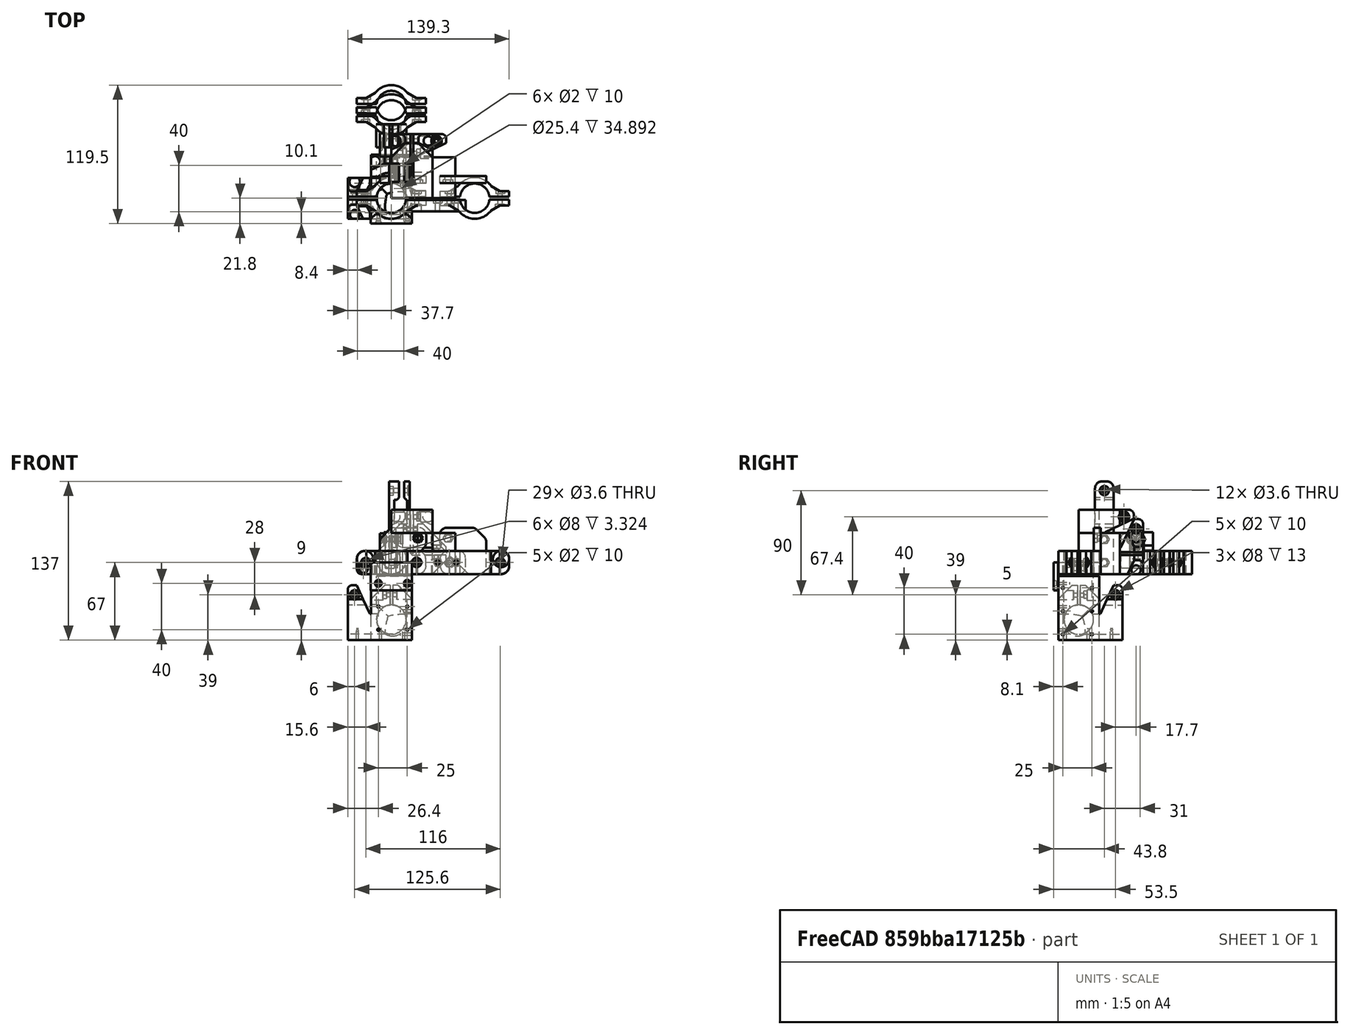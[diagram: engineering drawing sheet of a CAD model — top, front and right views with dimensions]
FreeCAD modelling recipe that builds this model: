
FCSTD DOCUMENT  (FreeCAD 0.19R23578 (Git))
Label: pipe_frame
License: All rights reserved
LicenseURL: http://en.wikipedia.org/wiki/All_rights_reserved
objects: PartDesign::FeatureBase×35, PartDesign::Body×35, Part::MultiFuse×32, Part::Cylinder×31, Part::Box×26, Part::Cut×16, App::Part×10, Part::Fillet×9, Part::Mirroring×8, Part::FeaturePython×7, Part::Chamfer×6, Part::Extrusion×3, Spreadsheet::Sheet×2, Part::Compound×2, Part::Sphere×1, Part::Cone×1
note: 212 computed .brp shape members not serialized (recipe doc carries the construction recipe); baked Part::Feature solids carry a one-line shape summary decoded from their .brp

FEATURE [Part::Cylinder] Cylinder  label="pipe 25mm"
  Angle = 360
  AttacherType = Attacher::AttachEngine3D
  Height = 300
  Radius = 12.7
  expr: Radius = <<p>>.pipe_r
FEATURE [Part::Box] Box001  label="Cube X"
  AttacherType = Attacher::AttachEngine3D
  Height = 35.4
  Length = 20
  Placement = pos=(35.4,0,0) rot=(0,0,1;0rad)
  Width = 35.4
  expr: Length = <<p>>.cube_extra_axis_sz
  expr: Width = <<p>>.cube_wall_sz
  expr: Height = <<p>>.cube_wall_sz
  expr: .Placement.Base.x = <<p>>.cube_wall_sz
FEATURE [Spreadsheet::Sheet] Spreadsheet  label="p"
  cells = A1=pipe_r; B1(pipe_r)=12.7; A2=corner_wall; B2(corner_wall)=5; A3=cube_wall_sz; B3(cube_wall_sz)==2 * pipe_r + 2 * corner_wall; A4=cube_extra_axis_sz; B4(cube_extra_axis_sz)=20; A5=cube_cut_along_sz; B5(cube_cut_along_sz)=2.4; A6=cube_cut_across_sz; B6(cube_cut_across_sz)=30; A7=bolt_squeeze_wall; B7(bolt_squeeze_wall)=5; A8=bolt_squeeze_height; B8(bolt_squeeze_height)=12; A9=profile_10x20_hole_width; B9(profile_10x20_hole_width)=10; A10=profile_10x20_hole_length; B10(profile_10x20_hole_length)=20; A11=cube_profile_width; B11(cube_profile_width)=10; A12=cube_profile_length; B12(cube_profile_length)=20; A13=cube_profile_attachment_height; B13(cube_profile_attachment_height)=40; A14=wall; B14(wall)=3; A15=cube_profile_attachment_length; B15(cube_profile_attachment_length)=16; A16=blocker_circumference; B16(blocker_circumference)==pipe_r * 2 * pi; A17=blocker_r; B17(blocker_r)==pipe_r; A18=blocker_angle; B18(blocker_angle)==blocker_circumference / (blocker_r * 2 * pi / 360) - 30
FEATURE [PartDesign::FeatureBase] Clone
  BaseFeature = -> Cylinder
FEATURE [PartDesign::Body] Body  label="pipe 25mm Z clone"
  BaseFeature = -> Cylinder
  Group = -> [Clone]
  Origin = -> Origin001
  Placement = pos=(17.7,17.7,17.7) rot=(0,0,1;0rad)
  Tip = -> Clone
  expr: .Placement.Base.y = <<p>>.cube_wall_sz / 2
  expr: .Placement.Base.x = <<p>>.cube_wall_sz / 2
  expr: .Placement.Base.z = <<p>>.cube_wall_sz / 2
FEATURE [PartDesign::FeatureBase] Clone001
  BaseFeature = -> Cylinder
FEATURE [PartDesign::Body] Body001  label="pipe 25mm X clone"
  BaseFeature = -> Cylinder
  Group = -> [Clone001]
  Origin = -> Origin002
  Placement = pos=(17.7,17.7,17.7) rot=(0,1,0;1.5708rad)
  Tip = -> Clone001
  expr: .Placement.Base.x = <<p>>.cube_wall_sz / 2
  expr: .Placement.Base.y = <<p>>.cube_wall_sz / 2
  expr: .Placement.Base.z = <<p>>.cube_wall_sz / 2
FEATURE [PartDesign::FeatureBase] Clone002
  BaseFeature = -> Cylinder
FEATURE [PartDesign::Body] Body002  label="pipe 25mm Y clone"
  BaseFeature = -> Cylinder
  Group = -> [Clone002]
  Origin = -> Origin003
  Placement = pos=(17.7,17.7,17.7) rot=(-1,0,0;1.5708rad)
  Tip = -> Clone002
  expr: .Placement.Base.x = <<p>>.cube_wall_sz / 2
  expr: .Placement.Base.y = <<p>>.cube_wall_sz / 2
  expr: .Placement.Base.z = <<p>>.cube_wall_sz / 2
FEATURE [Part::Box] Box002  label="Cube Central"
  AttacherType = Attacher::AttachEngine3D
  Height = 35.4
  Length = 35.4
  Width = 35.4
  expr: Length = <<p>>.cube_wall_sz
  expr: Width = <<p>>.cube_wall_sz
  expr: Height = <<p>>.cube_wall_sz
FEATURE [Part::Box] Box003  label="Cube Y"
  AttacherType = Attacher::AttachEngine3D
  Height = 35.4
  Length = 35.4
  Placement = pos=(0,35.4,0) rot=(0,0,1;0rad)
  Width = 20
  expr: Width = <<p>>.cube_extra_axis_sz
  expr: Height = <<p>>.cube_wall_sz
  expr: Length = <<p>>.cube_wall_sz
  expr: .Placement.Base.y = <<p>>.cube_wall_sz
FEATURE [Part::Box] Box004  label="Cube Z"
  AttacherType = Attacher::AttachEngine3D
  Height = 20
  Length = 35.4
  Placement = pos=(0,0,35.4) rot=(0,0,1;0rad)
  Width = 35.4
  expr: Width = <<p>>.cube_wall_sz
  expr: Height = <<p>>.cube_extra_axis_sz
  expr: .Placement.Base.z = <<p>>.cube_wall_sz
  expr: Length = <<p>>.cube_wall_sz
FEATURE [Part::Box] Box005  label="Cube X body"
  AttacherType = Attacher::AttachEngine3D
  Height = 35.4
  Length = 20
  Width = 35.4
  expr: Length = <<p>>.cube_extra_axis_sz
  expr: Width = <<p>>.cube_wall_sz
  expr: Height = <<p>>.cube_wall_sz
FEATURE [Part::Box] Box006  label="Cube X cut across"
  AttacherType = Attacher::AttachEngine3D
  Height = 35.4
  Length = 30
  Placement = pos=(0,0,22.7) rot=(0,0,1;0rad)
  Width = 35.4
  expr: Width = <<p>>.cube_wall_sz
  expr: Height = <<p>>.cube_wall_sz
  expr: .Placement.Base.z = <<p>>.cube_wall_sz / 2 + 5
  expr: Length = <<p>>.cube_cut_across_sz
FEATURE [Part::Box] Box007  label="Cube X cut along"
  AttacherType = Attacher::AttachEngine3D
  Height = 35.4
  Length = 20
  Placement = pos=(0,16.5,17.7) rot=(0,0,1;0rad)
  Width = 2.4
  expr: Height = <<p>>.cube_wall_sz
  expr: .Placement.Base.z = <<p>>.cube_wall_sz / 2
  expr: Length = <<p>>.cube_extra_axis_sz
  expr: Width = Spreadsheet.cube_cut_along_sz
  expr: .Placement.Base.y = (<<p>>.cube_wall_sz - Spreadsheet.cube_cut_along_sz) / 2
FEATURE [Part::Box] Box008  label="Cube X block along"
  AttacherType = Attacher::AttachEngine3D
  Height = 29.7
  Length = 20
  Placement = pos=(0,0,17.7) rot=(0,0,1;0rad)
  Width = 35.4
  expr: .Placement.Base.z = p001.cube_wall_sz / 2
  expr: Height = <<p>>.cube_wall_sz / 2 + <<p>>.bolt_squeeze_height
  expr: Length = <<p>>.cube_extra_axis_sz
  expr: Width = <<p>>.cube_wall_sz
FEATURE [Part::Extrusion] Extrude003  label="m3 nut hole"
  Dir = (0,0,1)
  DirMode = 2
  FaceMakerClass = Part::FaceMakerBullseye
  LengthFwd = 20
  LengthRev = 0
  Solid = true
  Symmetric = false
FEATURE [PartDesign::FeatureBase] Clone018
  BaseFeature = -> Extrude003
FEATURE [PartDesign::Body] Body020  label="m3 nut hole clone"
  BaseFeature = -> Extrude003
  Group = -> [Clone018]
  Origin = -> Origin040
  Placement = pos=(0,42,0) rot=(1,0,0;1.5708rad)
  Tip = -> Clone018
FEATURE [Part::Cylinder] Cylinder079  label="m3 bolt hole"
  Angle = 360
  AttacherType = Attacher::AttachEngine3D
  Height = 30
  Placement = pos=(0,0,0) rot=(-1,0,0;1.5708rad)
  Radius = 1.8
FEATURE [Part::Sphere] Sphere
  Angle1 = -90
  Angle2 = 90
  Angle3 = 360
  AttacherType = Attacher::AttachEngine3D
  Placement = pos=(16.635,16.635,16.25) rot=(0,0,1;0rad)
  Radius = 12.7
  expr: Radius = <<p>>.pipe_r
FEATURE [Part::MultiFuse] Fusion001  label="pipe fusion"
  Shapes = -> [Body,Body001,Body002,Sphere]
FEATURE [PartDesign::FeatureBase] Clone003
  BaseFeature = -> Fusion001
FEATURE [PartDesign::Body] Body003  label="pipe fusion clone"
  BaseFeature = -> Fusion001
  Group = -> [Clone003]
  Origin = -> Origin004
  Tip = -> Clone003
FEATURE [Part::Cylinder] Cylinder080  label="m3 screw hole"
  Angle = 360
  AttacherType = Attacher::AttachEngine3D
  Height = 10
  Placement = pos=(0,0,0) rot=(0,1,0;1.5708rad)
  Radius = 1
FEATURE [Part::FeaturePython] Array  label="ZY screw hole array"  # Draft array (typed FeaturePython)
  Angle = 360
  ArrayType = 0
  Axis = (0,0,1)
  Base = -> Cylinder080
  Center = (0,0,0)
  Fuse = false
  IntervalAxis = (0,0,0)
  IntervalX = (1,0,0)
  IntervalY = (0,25,0)
  IntervalZ = (0,0,20)
  NumberPolar = 1
  NumberX = 1
  NumberY = 2
  NumberZ = 3
  Placement = pos=(0,4,35) rot=(0,0,1;0rad)
  expr: .IntervalY.y = 25
FEATURE [PartDesign::FeatureBase] Clone024
  BaseFeature = -> Array
  Placement = pos=(0,4,23) rot=(0,0,1;0rad)
FEATURE [PartDesign::Body] Body026  label="Z screw hole array clone"
  BaseFeature = -> Array
  Group = -> [Clone024]
  Origin = -> Origin046
  Placement = pos=(0,0,-14) rot=(0,0,1;0rad)
  Tip = -> Clone024
FEATURE [PartDesign::FeatureBase] Clone025
  BaseFeature = -> Array
  Placement = pos=(0,4,23) rot=(0,0,1;0rad)
FEATURE [PartDesign::Body] Body027  label="Z screw hole array clone001"
  BaseFeature = -> Array
  Group = -> [Clone025]
  Origin = -> Origin047
  Placement = pos=(33,-7e-15,-18) rot=(0,0,1;1.5708rad)
  Tip = -> Clone025
FEATURE [Part::Cylinder] Cylinder081  label="m3 screw hole001"
  Angle = 360
  AttacherType = Attacher::AttachEngine3D
  Height = 10
  Radius = 1
FEATURE [Part::FeaturePython] Array001  label="bottom hole array"  # Draft array (typed FeaturePython)
  Angle = 360
  ArrayType = 0
  Axis = (0,0,1)
  Base = -> Cylinder081
  Center = (0,0,0)
  Fuse = false
  IntervalAxis = (0,0,0)
  IntervalX = (20,0,0)
  IntervalY = (0,20,0)
  IntervalZ = (0,0,1)
  NumberPolar = 1
  NumberX = 3
  NumberY = 3
  NumberZ = 1
  Placement = pos=(6,7,0) rot=(0,0,1;0rad)
FEATURE [Part::MultiFuse] Fusion057  label="pipe extraction fusion"
  Shapes = -> [Body003,Body026,Body027,Array001]
FEATURE [Part::Cylinder] Cylinder082  label="bolt head cylinder"
  Angle = 360
  AttacherType = Attacher::AttachEngine3D
  Height = 20
  Placement = pos=(0,-7,4.9e-15) rot=(-1,0,0;1.5708rad)
  Radius = 4
  expr: .Placement.Base.y = 2 - 2 - 2 - <<p>>.bolt_squeeze_wall
FEATURE [Part::Chamfer] Chamfer  label="Cube X block along chamfer"
  Base = -> Box008
  Edges = 2 edges r=12: [Edge10,Edge12]
FEATURE [Part::Fillet] Fillet  label="Cube X block along fillet"
  Base = -> Chamfer
  Edges = 2 edges r=4: [Edge4,Edge15]
FEATURE [Part::MultiFuse] Fusion002  label="Cube X fusion"
  Shapes = -> [Box005,Fillet]
FEATURE [Part::Box] Box009  label="Cube X cut across extract"
  AttacherType = Attacher::AttachEngine3D
  Height = 100
  Length = 30
  Placement = pos=(-1.55228,0,17.7) rot=(0,1,0;0.436332rad)
  Width = 35.4
  expr: Width = <<p>>.cube_wall_sz
  expr: .Placement.Base.z = <<p>>.cube_wall_sz / 2
  expr: Length = <<p>>.cube_cut_across_sz
FEATURE [Part::Cut] Cut002  label="Cube X cut across extracted"
  Base = -> Box006
  Tool = -> Box009
FEATURE [Part::Cylinder] Cylinder083  label="outer wall"
  Angle = 160
  AttacherType = Attacher::AttachEngine3D
  Height = 20
  Placement = pos=(0,0,0) rot=(0,0,1;0.174533rad)
  Radius = 17.7
  expr: Radius = <<p>>.pipe_r + <<p>>.corner_wall
FEATURE [Part::Cylinder] Cylinder084  label="pile extraction"
  Angle = 360
  AttacherType = Attacher::AttachEngine3D
  Height = 20
  Placement = pos=(0,0,0) rot=(0,0,1;0.174533rad)
  Radius = 12.7
  expr: Radius = <<p>>.pipe_r
FEATURE [Part::Box] Box  label="Cube"
  AttacherType = Attacher::AttachEngine3D
  Height = 20
  Length = 59.4
  Placement = pos=(-29.7,1.2,0) rot=(0,0,1;0rad)
  Width = 5
  expr: Width = <<p>>.bolt_squeeze_wall
  expr: Length = (<<p>>.pipe_r + <<p>>.corner_wall + <<p>>.bolt_squeeze_height) * 2
  expr: .Placement.Base.x = -(<<p>>.pipe_r + <<p>>.corner_wall + <<p>>.bolt_squeeze_height)
  expr: .Placement.Base.y = Spreadsheet.cube_cut_along_sz / 2
FEATURE [Part::Fillet] Fillet001
  Base = -> Box
  Edges = 4 edges r=7: [Edge2,Edge4,Edge6,Edge8]
FEATURE [Part::MultiFuse] Fusion058
  Shapes = -> [Cylinder083,Fillet001]
FEATURE [Part::Cut] Cut003
  Base = -> Fusion058
  Tool = -> Cylinder084
FEATURE [Part::Extrusion] Extrude002  label="m4 nut hole"
  Dir = (0,0,1)
  DirMode = 2
  FaceMakerClass = Part::FaceMakerBullseye
  LengthFwd = 20
  LengthRev = 0
  Solid = true
  Symmetric = false
FEATURE [Part::MultiFuse] Fusion052  label="m4 bolt nut fusion"
  Placement = pos=(23,6,31) rot=(0,0,1;0rad)
FEATURE [Part::Box] Box011  label="Cube002"
  AttacherType = Attacher::AttachEngine3D
  Height = 40
  Length = 40
  Placement = pos=(-10,13,0) rot=(0,0,1;0rad)
  Width = 6
FEATURE [Part::Box] Box012  label="Cube003"
  AttacherType = Attacher::AttachEngine3D
  Height = 60
  Length = 30
  Placement = pos=(-2.22183,13,-7.77817) rot=(0,1,0;0.785398rad)
  Width = 6
FEATURE [Part::Cut] Cut006
  Base = -> Box011
  Tool = -> Box012
FEATURE [Part::Chamfer] Chamfer001
  Base = -> Cut006
  Edges = 1 edges r=10: [Edge2]
FEATURE [Part::Fillet] Fillet002
  Base = -> Chamfer001
  Edges = 6 edges r=6: [Edge2,Edge3,Edge10,Edge13,Edge17,Edge18]
FEATURE [Part::Cut] Cut005  label="side block cut"
  Base = -> Fillet002
  Tool = -> Fusion052
FEATURE [Part::Chamfer] Chamfer002
  Base = -> Cut003
  Edges = 2 edges r=5: [Edge20,Edge30]
FEATURE [Part::Mirroring] Part__Mirroring001  label="Cut003 (Mirror #2)"
  Base = (0,2.86102e-06,10)
  Normal = (0,1,-1.19209e-07)
  Source = -> Chamfer002
FEATURE [Part::MultiFuse] Fusion059
  Shapes = -> [Part__Mirroring001,Chamfer002]
FEATURE [Part::Cylinder] Cylinder085  label="nut cylinder"
  Angle = 360
  AttacherType = Attacher::AttachEngine3D
  Height = 20
  Placement = pos=(0,25,1.9e-14) rot=(-1,0,0;1.5708rad)
  Radius = 4.5
FEATURE [Part::MultiFuse] Fusion056  label="m3 bolt nut fusion"
  Shapes = -> [Cylinder079,Body020,Cylinder082,Cylinder085]
FEATURE [PartDesign::FeatureBase] Clone019
  BaseFeature = -> Fusion056
FEATURE [PartDesign::Body] Body021  label="m3 bolt nut fusion clone"
  BaseFeature = -> Fusion056
  Group = -> [Clone019]
  Origin = -> Origin041
  Placement = pos=(14,0,39) rot=(0,0,1;0rad)
  Tip = -> Clone019
FEATURE [Part::MultiFuse] Fusion003  label="Cube X hole fusion"
  Shapes = -> [Box007,Body021,Cut002]
FEATURE [Part::Cut] Cut001  label="Cube X cut"
  Base = -> Fusion002
  Tool = -> Fusion003
FEATURE [PartDesign::FeatureBase] Clone020
  BaseFeature = -> Cut001
FEATURE [PartDesign::Body] Body022  label="Cube X cut clone X"
  BaseFeature = -> Cut001
  Group = -> [Clone020]
  Origin = -> Origin042
  Placement = pos=(35.4,-8e-15,0) rot=(0,0,1;0rad)
  Tip = -> Clone020
  expr: .Placement.Base.x = <<p>>.cube_wall_sz
FEATURE [PartDesign::FeatureBase] Clone021
  BaseFeature = -> Cut001
FEATURE [PartDesign::Body] Body023  label="Cube X cut clone Y"
  BaseFeature = -> Cut001
  Group = -> [Clone021]
  Origin = -> Origin043
  Placement = pos=(35.4,35.4,3e-15) rot=(0,0,1;1.5708rad)
  Tip = -> Clone021
  expr: .Placement.Base.x = <<p>>.cube_wall_sz
  expr: .Placement.Base.y = <<p>>.cube_wall_sz
FEATURE [PartDesign::FeatureBase] Clone022
  BaseFeature = -> Cut001
FEATURE [PartDesign::Body] Body024  label="Cube X cut clone Z"
  BaseFeature = -> Cut001
  Group = -> [Clone022]
  Origin = -> Origin044
  Placement = pos=(-1.6e-14,-4e-15,35.4) rot=(0.57735,0.57735,0.57735;4.18879rad)
  Tip = -> Clone022
  expr: .Placement.Base.z = <<p>>.cube_wall_sz
FEATURE [Part::Mirroring] Part__Mirroring  label="Cube X cut (Mirror #1)"
  Base = (0,0,0)
  Normal = (0,1,0)
  Source = -> Cut001
FEATURE [PartDesign::FeatureBase] Clone023
  BaseFeature = -> Cut001
FEATURE [PartDesign::Body] Body025  label="Cube X cut clone Y001"
  BaseFeature = -> Cut001
  Group = -> [Clone023]
  Origin = -> Origin045
  Placement = pos=(0,35.4,0) rot=(0.57735,0.57735,0.57735;2.0944rad)
  Tip = -> Clone023
  expr: .Placement.Base.y = <<p>>.cube_wall_sz
FEATURE [PartDesign::FeatureBase] Clone026
  BaseFeature = -> Part__Mirroring
FEATURE [PartDesign::Body] Body028  label="Cube X cut (Mirror #1) Y"
  BaseFeature = -> Part__Mirroring
  Group = -> [Clone026]
  Origin = -> Origin048
  Placement = pos=(7e-15,35.4,0) rot=(0,0,1;1.5708rad)
  Tip = -> Clone026
  expr: .Placement.Base.y = <<p>>.cube_wall_sz
FEATURE [Part::MultiFuse] Fusion  label="corner fusion"
  Shapes = -> [Box002,Box004,Body022,Body028]
FEATURE [Part::Cut] Cut  label="pipe cut"
  Base = -> Fusion
  Tool = -> Fusion057
FEATURE [App::Part] Part  label="corner part"
  Group = -> [Box001,Box002,Box003,Box004,Fusion,Body003,Cut,Body022,Body023,Body024,Body025,Body026,Cut001,Fusion003,Part__Mirroring,Fusion001,Body021,Fusion002,Body002,Body001,Cylinder,Body,Box005,Box006,Box007,Box008,Sphere,Fillet,Fusion057,Body027,Cylinder081,Array001]
  Origin = -> Origin
FEATURE [PartDesign::FeatureBase] Clone028
  BaseFeature = -> Fusion056
FEATURE [PartDesign::Body] Body030  label="m3 bolt nut fusion clone002"
  BaseFeature = -> Fusion056
  Group = -> [Clone028]
  Origin = -> Origin051
  Placement = pos=(-22,0,10) rot=(0,0,1;0rad)
  Tip = -> Clone028
FEATURE [Part::Mirroring] Part__Mirroring002  label="m3 bolt nut fusion clone002 (Mirror #3)"
  Base = (9.53674e-07,17.5,10)
  Normal = (1,0,-1.19209e-07)
  Source = -> Body030
FEATURE [Part::MultiFuse] Fusion062  label="m3 bolt nut fusion002"
  Placement = pos=(0,-18,0) rot=(0,0,1;0rad)
  Shapes = -> [Part__Mirroring002,Body030]
FEATURE [Part::Cut] Cut004  label="tube block cut"
  Base = -> Fusion059
  Tool = -> Fusion062
FEATURE [Part::Compound] Compound  label="attach part compound"
  Links = -> [Cut004,Cut005]
FEATURE [PartDesign::FeatureBase] Clone029
  BaseFeature = -> Cut004
FEATURE [PartDesign::Body] Body031  label="tube block cut clone"
  BaseFeature = -> Cut004
  Group = -> [Clone029]
  Origin = -> Origin053
  Tip = -> Clone029
FEATURE [Part::Box] Box039  label="profile 20x10 holder cube"
  AttacherType = Attacher::AttachEngine3D
  Height = 35
  Length = 20
  Placement = pos=(-10,16,0) rot=(0,0,1;0rad)
  Width = 20
  expr: Length = 2 * <<p>>.corner_wall + <<p>>.profile_10x20_hole_width
  expr: .Placement.Base.x = -(2 * <<p>>.corner_wall + <<p>>.profile_10x20_hole_width) / 2
  expr: Height = <<p>>.corner_wall + <<p>>.profile_10x20_hole_length + 10
FEATURE [Part::Box] Box040  label="profile 20x10 extraction hole"
  AttacherType = Attacher::AttachEngine3D
  Height = 70
  Length = 10
  Placement = pos=(-5,16,5) rot=(0,0,1;0rad)
  Width = 50
  expr: Height = <<p>>.profile_10x20_hole_length + 50
  expr: .Placement.Base.z = <<p>>.corner_wall
  expr: Length = <<p>>.profile_10x20_hole_width
FEATURE [Part::Fillet] Fillet003
  Base = -> Box039
  Edges = 2 edges r=5: [Edge10,Edge12]
FEATURE [Part::Cylinder] Cylinder086  label="m3 bolt hole001"
  Angle = 360
  AttacherType = Attacher::AttachEngine3D
  Height = 30
  Placement = pos=(0,0,0) rot=(-1,0,0;1.5708rad)
  Radius = 1.8
FEATURE [PartDesign::FeatureBase] Clone030
  BaseFeature = -> Extrude003
FEATURE [PartDesign::Body] Body032  label="m3 nut hole clone001"
  BaseFeature = -> Extrude003
  Group = -> [Clone030]
  Origin = -> Origin054
  Placement = pos=(0,42,0) rot=(1,0,0;1.5708rad)
  Tip = -> Clone030
FEATURE [Part::Cylinder] Cylinder087  label="bolt head cylinder002"
  Angle = 360
  AttacherType = Attacher::AttachEngine3D
  Height = 20
  Placement = pos=(0,-14,3e-15) rot=(-1,0,0;1.5708rad)
  Radius = 4
FEATURE [Part::Cylinder] Cylinder088  label="bolt head cylinder003"
  Angle = 360
  AttacherType = Attacher::AttachEngine3D
  Height = 20
  Placement = pos=(0,25,3.48e-14) rot=(-1,0,0;1.5708rad)
  Radius = 4.5
FEATURE [Part::MultiFuse] Fusion063  label="m3 bolt nut fusion003"
  Shapes = -> [Cylinder086,Body032,Cylinder087,Cylinder088]
FEATURE [PartDesign::FeatureBase] Clone031
  BaseFeature = -> Fusion063
FEATURE [PartDesign::Body] Body033  label="m3 bolt nut fusion003 clone"
  BaseFeature = -> Fusion063
  Group = -> [Clone031]
  Origin = -> Origin055
  Placement = pos=(14,27,30) rot=(0,0,1;1.5708rad)
  Tip = -> Clone031
  expr: .Placement.Base.z = <<p>>.corner_wall + <<p>>.profile_10x20_hole_length + 5
FEATURE [App::Part] Part003  label="m3 bold nut fusion part"
  Group = -> [Cylinder086,Body032,Cylinder087,Cylinder088,Fusion063]
  Origin = -> Origin056
FEATURE [Part::MultiFuse] Fusion064  label="profile holder extraction fusion"
  Shapes = -> [Box040,Body033]
FEATURE [Part::Mirroring] Part__Mirroring004  label="attach part compound (Mirror #5)"
  Base = (36,0,0)
  Normal = (1,0,0)
  Source = -> Compound
FEATURE [App::Part] Part001  label="25mm_attach part"
  Group = -> [Cylinder083,Cylinder084,Cut003,Box,Fusion058,Fillet001,Part__Mirroring001,Fusion059,Body030,Cut004,Fusion052,Fillet002,Box011,Cut005,Chamfer001,Box012,Cut006,Part__Mirroring002,Fusion062,Compound,Chamfer002,Fusion056,Body020,Cylinder079,Cylinder082,Cylinder085,Part__Mirroring004]
  Origin = -> Origin049
FEATURE [Part::MultiFuse] Fusion065
  Shapes = -> [Fillet003,Body031]
FEATURE [Part::Cut] Cut007  label="profile holder cut"
  Base = -> Fusion065
  Tool = -> Fusion064
FEATURE [Part::Mirroring] Part__Mirroring003  label="profile holder cut (Mirror #4)"
  Base = (0,36,0)
  Normal = (0,1,0)
  Source = -> Cut007
FEATURE [App::Part] Part002  label="25mm side pipe attach part"
  Group = -> [Body031,Box039,Box040,Fillet003,Cut007,Body033,Fusion064,Part__Mirroring003,Fusion065]
  Origin = -> Origin052
FEATURE [Part::Box] Box042  label="attachment extraction"
  AttacherType = Attacher::AttachEngine3D
  Height = 40
  Length = 20
  Placement = pos=(20,5,0) rot=(0,0,1;0rad)
  Width = 4.3
  expr: Height = <<p>>.cube_profile_attachment_height
FEATURE [PartDesign::FeatureBase] Clone011
  BaseFeature = -> Extrude002
FEATURE [PartDesign::Body] Body013  label="m4 nut hole clone"
  BaseFeature = -> Extrude002
  Group = -> [Clone011]
  Placement = pos=(0,-10,0) rot=(-1,0,0;1.5708rad)
  Tip = -> Clone011
FEATURE [Part::Cylinder] Cylinder077  label="m4 bolt hole"
  Angle = 360
  AttacherType = Attacher::AttachEngine3D
  Height = 30
  Placement = pos=(0,0,0) rot=(-1,0,0;1.5708rad)
  Radius = 2.6
FEATURE [Part::MultiFuse] Fusion067  label="m4 bolt nut fusion001"
  Shapes = -> [Cylinder077,Body013]
FEATURE [Part::FeaturePython] Array001042  label="m4 bolt hole array"  # Draft array (typed FeaturePython)
  Angle = 360
  ArrayType = 0
  Axis = (0,0,1)
  Base = -> Fusion067
  Center = (0,0,0)
  Fuse = false
  IntervalAxis = (0,0,0)
  IntervalX = (1,0,0)
  IntervalY = (0,1,0)
  IntervalZ = (0,0,20)
  NumberPolar = 1
  NumberX = 1
  NumberY = 1
  NumberZ = 2
  Placement = pos=(13,25,10) rot=(0,0,1;1.5708rad)
FEATURE [Part::Box] Box041  label="attachment internal cube"
  AttacherType = Attacher::AttachEngine3D
  Height = 40
  Length = 21
  Placement = pos=(3,2.5,0) rot=(0,0,1;0rad)
  Width = 11
  expr: Length = <<p>>.cube_profile_length + 1
  expr: Width = <<p>>.cube_profile_width + 1
  expr: Height = <<p>>.cube_profile_attachment_height
  expr: .Placement.Base.x = <<p>>.wall
  expr: .Placement.Base.y = <<p>>.wall - 0.5
FEATURE [Part::Box] Box045  label="attachment external cube"
  AttacherType = Attacher::AttachEngine3D
  Height = 16
  Length = 40
  Width = 18
  expr: Length = <<p>>.cube_profile_length + 2 * <<p>>.wall + 14
  expr: Width = <<p>>.cube_profile_width + 2 * <<p>>.wall + 2
  expr: Height = <<p>>.cube_profile_attachment_length
FEATURE [PartDesign::FeatureBase] Clone033
  BaseFeature = -> Extrude002
FEATURE [PartDesign::Body] Body035  label="m4 nut hole clone001"
  BaseFeature = -> Extrude002
  Group = -> [Clone033]
  Placement = pos=(0,-10,0) rot=(-1,0,0;1.5708rad)
  Tip = -> Clone033
FEATURE [Part::Cylinder] Cylinder090  label="m4 bolt hole001"
  Angle = 360
  AttacherType = Attacher::AttachEngine3D
  Height = 30
  Placement = pos=(0,0,0) rot=(-1,0,0;1.5708rad)
  Radius = 2.6
FEATURE [Part::MultiFuse] Fusion068  label="m4 bolt nut fusion002"
  Shapes = -> [Cylinder090,Body035]
FEATURE [Part::FeaturePython] Array001045  label="m4 bolt hole array001"  # Draft array (typed FeaturePython)
  Angle = 360
  ArrayType = 0
  Axis = (0,0,1)
  Base = -> Fusion068
  Center = (0,0,0)
  Fuse = false
  IntervalAxis = (0,0,0)
  IntervalX = (1,0,0)
  IntervalY = (0,1,0)
  IntervalZ = (0,0,20)
  NumberPolar = 1
  NumberX = 1
  NumberY = 1
  NumberZ = 2
  Placement = pos=(13,22,10) rot=(0,0,1;1.5708rad)
FEATURE [Part::Box] Box046  label="frame attachment cube001"
  AttacherType = Attacher::AttachEngine3D
  Height = 40
  Length = 6
  Placement = pos=(-2,14,0) rot=(0,0,1;0rad)
  Width = 16
  expr: Height = <<p>>.cube_profile_attachment_height
  expr: Width = <<p>>.cube_profile_attachment_length
FEATURE [Part::Cut] Cut023014  label="frame attach cut"
  Base = -> Box046
  Tool = -> Array001045
FEATURE [Part::Cylinder] Cylinder091  label="m3 bolt hole003"
  Angle = 360
  AttacherType = Attacher::AttachEngine3D
  Height = 30
  Placement = pos=(0,0,0) rot=(-1,0,0;1.5708rad)
  Radius = 1.8
FEATURE [PartDesign::FeatureBase] Clone034
  BaseFeature = -> Extrude003
FEATURE [PartDesign::Body] Body036  label="m3 nut hole clone003"
  BaseFeature = -> Extrude003
  Group = -> [Clone034]
  Origin = -> Origin059
  Placement = pos=(0,42,0) rot=(1,0,0;1.5708rad)
  Tip = -> Clone034
FEATURE [Part::Cylinder] Cylinder092  label="bolt head cylinder004"
  Angle = 360
  AttacherType = Attacher::AttachEngine3D
  Height = 20
  Placement = pos=(0,-7,5e-15) rot=(-1,0,0;1.5708rad)
  Radius = 4
FEATURE [Part::Cylinder] Cylinder093  label="bolt head cylinder005"
  Angle = 360
  AttacherType = Attacher::AttachEngine3D
  Height = 20
  Placement = pos=(0,-7,3.32e-14) rot=(-1,0,0;1.5708rad)
  Radius = 4.5
  expr: .Placement.Base.y = 2 - 2 - 2 - <<p>>.bolt_squeeze_wall
FEATURE [Part::MultiFuse] Fusion070  label="m3 bolt nut fusion005"
  Shapes = -> [Cylinder091,Body036,Cylinder092,Cylinder093]
FEATURE [Spreadsheet::Sheet] Spreadsheet001  label="p0"
  cells = A1=pipe_r; B1(pipe_r)=12.7; A2=corner_wall; B2(corner_wall)=5; A3=cube_wall_sz; B3(cube_wall_sz)==2 * pipe_r + 2 * corner_wall; A4=cube_extra_axis_sz; B4(cube_extra_axis_sz)=20; A5=cube_cut_along_sz; B5(cube_cut_along_sz)=3; A6=cube_cut_across_sz; B6(cube_cut_across_sz)=30; A7=bolt_squeeze_wall; B7(bolt_squeeze_wall)=5; A8=bolt_squeeze_height; B8(bolt_squeeze_height)=12; A9=profile_10x20_hole_width; B9(profile_10x20_hole_width)=10; A10=profile_10x20_hole_length; B10(profile_10x20_hole_length)=20; A11=cube_profile_width; B11(cube_profile_width)=10; A12=cube_profile_length; B12(cube_profile_length)=20; A13=cube_profile_attachment_height; B13(cube_profile_attachment_height)=40; A14=wall; B14(wall)=3; A15=cube_profile_attachment_length; B15(cube_profile_attachment_length)=16
FEATURE [Part::Extrusion] Extrude004  label="m3 nut hole001"
  Dir = (0,0,1)
  DirMode = 2
  FaceMakerClass = Part::FaceMakerBullseye
  LengthFwd = 20
  LengthRev = 0
  Solid = true
  Symmetric = false
FEATURE [PartDesign::FeatureBase] Clone036
  BaseFeature = -> Extrude004
FEATURE [PartDesign::Body] Body038  label="m3 nut hole clone004"
  BaseFeature = -> Extrude004
  Group = -> [Clone036]
  Origin = -> Origin061
  Placement = pos=(0,42,0) rot=(1,0,0;1.5708rad)
  Tip = -> Clone036
FEATURE [Part::Cylinder] Cylinder094  label="m3 bolt hole004"
  Angle = 360
  AttacherType = Attacher::AttachEngine3D
  Height = 30
  Placement = pos=(0,0,0) rot=(-1,0,0;1.5708rad)
  Radius = 1.8
FEATURE [Part::Cylinder] Cylinder095  label="bolt head cylinder006"
  Angle = 360
  AttacherType = Attacher::AttachEngine3D
  Height = 20
  Placement = pos=(0,-7,4.9e-15) rot=(-1,0,0;1.5708rad)
  Radius = 4
  expr: .Placement.Base.y = 2 - 2 - 2 - <<p>>.bolt_squeeze_wall
FEATURE [Part::Cylinder] Cylinder096  label="outer wall001"
  Angle = 160
  AttacherType = Attacher::AttachEngine3D
  Height = 20
  Placement = pos=(0,0,0) rot=(0,0,1;0.174533rad)
  Radius = 17.7
  expr: Radius = <<p>>.pipe_r + <<p>>.corner_wall
FEATURE [Part::Cylinder] Cylinder097  label="pile extraction001"
  Angle = 360
  AttacherType = Attacher::AttachEngine3D
  Height = 20
  Placement = pos=(0,0,0) rot=(0,0,1;0.174533rad)
  Radius = 12.7
  expr: Radius = <<p>>.pipe_r
FEATURE [Part::Box] Box047  label="Cube004"
  AttacherType = Attacher::AttachEngine3D
  Height = 20
  Length = 59.4
  Placement = pos=(-29.7,1.5,0) rot=(0,0,1;0rad)
  Width = 5
  expr: Width = <<p>>.bolt_squeeze_wall
  expr: Length = (<<p>>.pipe_r + <<p>>.corner_wall + <<p>>.bolt_squeeze_height) * 2
  expr: .Placement.Base.x = -(<<p>>.pipe_r + <<p>>.corner_wall + <<p>>.bolt_squeeze_height)
  expr: .Placement.Base.y = Spreadsheet001.cube_cut_along_sz / 2
FEATURE [Part::Fillet] Fillet022
  Base = -> Box047
  Edges = 4 edges r=7: [Edge2,Edge4,Edge6,Edge8]
FEATURE [Part::MultiFuse] Fusion072
  Shapes = -> [Cylinder096,Fillet022]
FEATURE [Part::Cut] Cut023016
  Base = -> Fusion072
  Tool = -> Cylinder097
FEATURE [Part::Chamfer] Chamfer004
  Base = -> Cut023016
  Edges = 2 edges r=5: [Edge20,Edge30]
FEATURE [Part::Mirroring] Part__Mirroring005  label="Cut003 (Mirror #2)001"
  Base = (0,2.86102e-06,10)
  Normal = (0,1,-1.19209e-07)
  Source = -> Chamfer004
FEATURE [Part::MultiFuse] Fusion073
  Shapes = -> [Part__Mirroring005,Chamfer004]
FEATURE [Part::Cylinder] Cylinder098  label="nut cylinder001"
  Angle = 360
  AttacherType = Attacher::AttachEngine3D
  Height = 20
  Placement = pos=(0,25,1.9e-14) rot=(-1,0,0;1.5708rad)
  Radius = 4.5
FEATURE [Part::MultiFuse] Fusion071  label="m3 bolt nut fusion006"
  Shapes = -> [Cylinder094,Body038,Cylinder095,Cylinder098]
FEATURE [PartDesign::FeatureBase] Clone037
  BaseFeature = -> Fusion071
FEATURE [PartDesign::Body] Body039  label="m3 bolt nut fusion clone003"
  BaseFeature = -> Fusion071
  Group = -> [Clone037]
  Origin = -> Origin062
  Placement = pos=(-22,0,10) rot=(0,0,1;0rad)
  Tip = -> Clone037
FEATURE [Part::Mirroring] Part__Mirroring006  label="m3 bolt nut fusion clone002 (Mirror #3)001"
  Base = (9.53674e-07,17.5,10)
  Normal = (1,0,-1.19209e-07)
  Source = -> Body039
FEATURE [Part::MultiFuse] Fusion074  label="m3 bolt nut fusion007"
  Placement = pos=(0,-18,0) rot=(0,0,1;0rad)
  Shapes = -> [Part__Mirroring006,Body039]
FEATURE [Part::Cut] Cut023015  label="tube block cut001"
  Base = -> Fusion073
  Tool = -> Fusion074
FEATURE [PartDesign::FeatureBase] Clone038
  BaseFeature = -> Cut023015
FEATURE [PartDesign::Body] Body040  label="tube block cut clone001"
  BaseFeature = -> Cut023015
  Group = -> [Clone038]
  Origin = -> Origin064
  Tip = -> Clone038
FEATURE [Part::Cylinder] Cylinder099  label="m3 bolt hole005"
  Angle = 360
  AttacherType = Attacher::AttachEngine3D
  Height = 30
  Placement = pos=(0,0,0) rot=(-1,0,0;1.5708rad)
  Radius = 1.8
FEATURE [PartDesign::FeatureBase] Clone039
  BaseFeature = -> Extrude004
FEATURE [PartDesign::Body] Body041  label="m3 nut hole clone005"
  BaseFeature = -> Extrude004
  Group = -> [Clone039]
  Origin = -> Origin065
  Placement = pos=(0,42,0) rot=(1,0,0;1.5708rad)
  Tip = -> Clone039
FEATURE [Part::Cylinder] Cylinder100  label="bolt head cylinder007"
  Angle = 360
  AttacherType = Attacher::AttachEngine3D
  Height = 20
  Placement = pos=(0,-6,4.8e-15) rot=(-1,0,0;1.5708rad)
  Radius = 4
FEATURE [Part::Cylinder] Cylinder101  label="bolt head cylinder008"
  Angle = 360
  AttacherType = Attacher::AttachEngine3D
  Height = 20
  Placement = pos=(0,25,3.48e-14) rot=(-1,0,0;1.5708rad)
  Radius = 4.5
FEATURE [Part::MultiFuse] Fusion075  label="m3 bolt nut fusion008"
  Shapes = -> [Cylinder099,Body041,Cylinder100,Cylinder101]
FEATURE [PartDesign::FeatureBase] Clone040
  BaseFeature = -> Fusion075
FEATURE [PartDesign::Body] Body042  label="m3 bolt nut fusion003 clone001"
  BaseFeature = -> Fusion075
  Group = -> [Clone040]
  Origin = -> Origin066
  Placement = pos=(18,27,30) rot=(0,0,1;1.5708rad)
  Tip = -> Clone040
FEATURE [Part::Cylinder] Cylinder102  label="cylinder 16mm"
  Angle = 360
  AttacherType = Attacher::AttachEngine3D
  Height = 50
  Placement = pos=(0,16,13) rot=(-1,0,0;1.5708rad)
  Radius = 8
FEATURE [Part::Cylinder] Cylinder103  label="cylinder 16mm holder"
  Angle = 360
  AttacherType = Attacher::AttachEngine3D
  Height = 20
  Placement = pos=(0,16,13) rot=(-1,0,0;1.5708rad)
  Radius = 13
  expr: Radius = 8 + <<p>>.corner_wall
FEATURE [Part::Box] Box048  label="squeeze cube"
  AttacherType = Attacher::AttachEngine3D
  Height = 12
  Length = 12.4
  Placement = pos=(-6.5,16,24) rot=(0,0,1;0rad)
  Width = 20
  expr: Height = <<p>>.bolt_squeeze_height
  expr: Length = 2 * <<p>>.bolt_squeeze_wall + <<p>>.cube_cut_along_sz
FEATURE [Part::MultiFuse] Fusion077
  Shapes = -> [Body040,Cylinder103,Box048]
FEATURE [Part::Box] Box049  label="squeeze cut cube"
  AttacherType = Attacher::AttachEngine3D
  Height = 22
  Length = 2.4
  Placement = pos=(-1.5,16,20) rot=(0,0,1;0rad)
  Width = 20
  expr: Height = <<p>>.bolt_squeeze_height + 10
  expr: Length = <<p>>.cube_cut_along_sz
FEATURE [Part::MultiFuse] Fusion076  label="profile holder extraction fusion001"
  Shapes = -> [Body042,Cylinder102,Box049]
FEATURE [Part::Cut] Cut023017  label="profile holder cut001"
  Base = -> Fusion077
  Tool = -> Fusion076
FEATURE [Part::Mirroring] Part__Mirroring007  label="profile holder cut (Mirror #4)001"
  Base = (0,40,0)
  Normal = (0,1,0)
  Source = -> Cut023017
FEATURE [App::Part] Part005  label="25mm side pipe 10mm attach part"
  Group = -> [Body040,Cut023017,Body042,Fusion076,Part__Mirroring007,Fusion077]
  Origin = -> Origin063
FEATURE [PartDesign::FeatureBase] Clone041
  BaseFeature = -> Cut023015
FEATURE [PartDesign::Body] Body043  label="tube block cut001 clone"
  BaseFeature = -> Cut023015
  Group = -> [Clone041]
  Origin = -> Origin067
  Tip = -> Clone041
FEATURE [Part::Box] Box050  label="Cube005"
  AttacherType = Attacher::AttachEngine3D
  Height = 20
  Length = 50
  Placement = pos=(14,-11.5,0) rot=(0,0,1;0rad)
  Width = 10
FEATURE [PartDesign::FeatureBase] Clone042
  BaseFeature = -> Fusion074
  Placement = pos=(0,-18,0) rot=(0,0,1;0rad)
FEATURE [PartDesign::Body] Body044  label="m3 bolt nut fusion007 clone"
  BaseFeature = -> Fusion074
  Group = -> [Clone042]
  Origin = -> Origin069
  Tip = -> Clone042
FEATURE [PartDesign::FeatureBase] Clone043
  BaseFeature = -> Fusion070
FEATURE [PartDesign::Body] Body045  label="m3 bolt nut fusion005 clone001"
  BaseFeature = -> Fusion070
  Group = -> [Clone043]
  Origin = -> Origin070
  Placement = pos=(40,-26,10) rot=(0,0,1;0rad)
  Tip = -> Clone043
FEATURE [Part::Fillet] Fillet023
  Base = -> Box050
  Edges = 2 edges r=6: [Edge6,Edge8]
FEATURE [Part::FeaturePython] Array001046  label="m3 bolt nut fusion005 clone001 array"  # Draft array (typed FeaturePython)
  Angle = 360
  ArrayType = 0
  Axis = (0,0,1)
  Base = -> Body045
  Center = (0,0,0)
  Fuse = false
  IntervalAxis = (0,0,0)
  IntervalX = (16,0,0)
  IntervalY = (0,1,0)
  IntervalZ = (0,0,1)
  NumberPolar = 1
  NumberX = 2
  NumberY = 1
  NumberZ = 1
FEATURE [Part::MultiFuse] Fusion079
  Shapes = -> [Body044,Array001046]
FEATURE [Part::Cut] Cut023018
  Base = -> Fillet023
  Tool = -> Fusion079
FEATURE [Part::MultiFuse] Fusion078  label="bottom attach fusion"
  Shapes = -> [Body043,Cut023018]
FEATURE [App::Part] Part006  label="bottom attach part"
  Group = -> [Body043,Box050,Fusion078,Cut023018,Fillet023]
  Origin = -> Origin068
FEATURE [PartDesign::FeatureBase] Clone046
  BaseFeature = -> Compound
FEATURE [PartDesign::Body] Body048  label="attach part clone"
  BaseFeature = -> Compound
  Group = -> [Clone046]
  Origin = -> Origin073
  Tip = -> Clone046
FEATURE [Part::Cylinder] Cylinder104  label="outer wall002"
  Angle = 330
  AttacherType = Attacher::AttachEngine3D
  Height = 10
  Placement = pos=(0,0,0) rot=(0,0,1;3.33358rad)
  Radius = 17.7
  expr: Radius = <<p>>.blocker_r + <<p>>.corner_wall
  expr: Angle = <<p>>.blocker_angle
  expr: .Placement.Rotation.Angle = -<<p>>.blocker_angle / 2 - 4
FEATURE [Part::Box] Box051  label="Cube006"
  AttacherType = Attacher::AttachEngine3D
  Height = 10
  Length = 29.7
  Placement = pos=(-29.7,1.2,0) rot=(0,0,1;0rad)
  Width = 5
  expr: Width = <<p>>.bolt_squeeze_wall
  expr: Length = <<p>>.pipe_r + <<p>>.corner_wall + <<p>>.bolt_squeeze_height
  expr: .Placement.Base.y = Spreadsheet.cube_cut_along_sz / 2
  expr: .Placement.Base.x = -(<<p>>.pipe_r + <<p>>.corner_wall + <<p>>.bolt_squeeze_height)
FEATURE [Part::Fillet] Fillet024
  Base = -> Box051
  Edges = 2 edges r=4: [Edge2,Edge4]
  Placement = pos=(0,1,0) rot=(0,0,1;0rad)
FEATURE [Part::Cylinder] Cylinder105  label="pile extraction002"
  Angle = 360
  AttacherType = Attacher::AttachEngine3D
  Height = 20
  Placement = pos=(0,0,0) rot=(0,0,1;0.174533rad)
  Radius = 12.7
  expr: Radius = <<p>>.blocker_r
FEATURE [PartDesign::FeatureBase] Clone047
  BaseFeature = -> Fusion071
FEATURE [PartDesign::Body] Body049  label="m3 bolt nut fusion006 clone"
  BaseFeature = -> Fusion071
  Group = -> [Clone047]
  Origin = -> Origin075
  Placement = pos=(-24,-17.5,5) rot=(0,0,1;0rad)
  Tip = -> Clone047
FEATURE [Part::Cylinder] Cylinder106  label="m3 bolt hole006"
  Angle = 360
  AttacherType = Attacher::AttachEngine3D
  Height = 30
  Placement = pos=(0,0,0) rot=(-1,0,0;1.5708rad)
  Radius = 1.8
FEATURE [PartDesign::FeatureBase] Clone048
  BaseFeature = -> Extrude003
FEATURE [PartDesign::Body] Body050  label="m3 nut hole clone006"
  BaseFeature = -> Extrude003
  Group = -> [Clone048]
  Origin = -> Origin076
  Placement = pos=(0,45,0) rot=(1,0,0;1.5708rad)
  Tip = -> Clone048
FEATURE [Part::Cylinder] Cylinder107  label="bolt head cylinder009"
  Angle = 360
  AttacherType = Attacher::AttachEngine3D
  Height = 20
  Placement = pos=(0,-7,5e-15) rot=(-1,0,0;1.5708rad)
  Radius = 4
FEATURE [Part::MultiFuse] Fusion082  label="m3 bolt nut fusion009"
  Shapes = -> [Cylinder106,Body050,Cylinder107]
FEATURE [Part::FeaturePython] Array001044  label="m3 bolt hole array"  # Draft array (typed FeaturePython)
  Angle = 360
  ArrayType = 0
  Axis = (0,0,1)
  Base = -> Fusion082
  Center = (0,0,0)
  Fuse = false
  IntervalAxis = (0,0,0)
  IntervalX = (1,0,0)
  IntervalY = (0,1,0)
  IntervalZ = (0,0,20)
  NumberPolar = 1
  NumberX = 1
  NumberY = 1
  NumberZ = 2
  Placement = pos=(32,-11,8) rot=(0,0,1;0rad)
FEATURE [Part::MultiFuse] Fusion051  label="attachment extraction fusion"
  Shapes = -> [Box041,Array001042,Box042,Array001044]
FEATURE [Part::Cut] Cut023013  label="profile attachment cut"
  Base = -> Box045
  Tool = -> Fusion051
FEATURE [Part::Fillet] Fillet021  label="profile attachment fillet"
  Base = -> Cut023013
  Edges = 4 edges r=6: [Edge10,Edge18,Edge27,Edge35]
FEATURE [Part::Chamfer] Chamfer003  label="profile attachment chamber"
  Base = -> Fillet021
  Edges = 2 edges r=2: [Edge49,Edge55]
  Placement = pos=(16,30,40) rot=(0.57735,-0.57735,0.57735;2.0944rad)
FEATURE [Part::MultiFuse] Fusion069  label="profile 20x10 attachment fusion"
  Shapes = -> [Chamfer003,Cut023014]
FEATURE [App::Part] Part004  label="profile 20x10 attachment part"
  Group = -> [Extrude002,Box046,Body035,Fusion068,Cylinder090,Array001045,Cut023014,Extrude003,Box042,Box041,Body013,Cylinder077,Cut023013,Array001044,Array001042,Fillet021,Fusion067,Box045,Fusion051,Chamfer003,Fusion069,Cylinder106,Body050,Cylinder107,Fusion082]
  Origin = -> Origin058
FEATURE [Part::Box] Box052  label="Cube007"
  AttacherType = Attacher::AttachEngine3D
  Height = 10
  Length = 29.7
  Placement = pos=(-29.7,1.2,0) rot=(0,0,1;0rad)
  Width = 5
  expr: Width = <<p>>.bolt_squeeze_wall
  expr: Length = <<p>>.pipe_r + <<p>>.corner_wall + <<p>>.bolt_squeeze_height
  expr: .Placement.Base.y = Spreadsheet.cube_cut_along_sz / 2
  expr: .Placement.Base.x = -(<<p>>.pipe_r + <<p>>.corner_wall + <<p>>.bolt_squeeze_height)
FEATURE [Part::Fillet] Fillet025
  Base = -> Box052
  Edges = 2 edges r=4: [Edge2,Edge4]
  Placement = pos=(0,-8,0) rot=(0,0,1;0rad)
FEATURE [Part::MultiFuse] Fusion080
  Shapes = -> [Cylinder104,Fillet025,Fillet024]
FEATURE [Part::MultiFuse] Fusion083
  Shapes = -> [Cylinder105,Body049]
FEATURE [Part::Cut] Cut023019  label="blocker cut"
  Base = -> Fusion080
  Tool = -> Fusion083
FEATURE [App::Part] Part007  label="blocker part"
  Group = -> [Cut023019]
  Origin = -> Origin074
FEATURE [PartDesign::FeatureBase] Clone049
  BaseFeature = -> Cut023019
FEATURE [PartDesign::Body] Body051  label="blocker part clone"
  BaseFeature = -> Cut023019
  Group = -> [Clone049]
  Origin = -> Origin077
  Tip = -> Clone049
FEATURE [PartDesign::FeatureBase] Clone050
  BaseFeature = -> Cut
FEATURE [PartDesign::Body] Body052  label="corner part clone"
  BaseFeature = -> Cut
  Group = -> [Clone050]
  Origin = -> Origin079
  Placement = pos=(17.8,-17.7,-57) rot=(0,0,1;1.5708rad)
  Tip = -> Clone050
FEATURE [Part::Box] Box053  label="Cube008"
  AttacherType = Attacher::AttachEngine3D
  Height = 24
  Length = 35.4
  Placement = pos=(-17.7,-21.8,-14) rot=(0,0,1;0rad)
  Width = 4
  expr: Length = <<p>>.cube_wall_sz
  expr: .Placement.Base.x = -<<p>>.cube_wall_sz / 2
FEATURE [Part::Box] Box054  label="Cube009"
  AttacherType = Attacher::AttachEngine3D
  Height = 10
  Length = 35.4
  Placement = pos=(-17.7,-21.8,0) rot=(0,0,1;0rad)
  Width = 8
  expr: Length = <<p>>.cube_wall_sz
  expr: .Placement.Base.x = -<<p>>.cube_wall_sz / 2
FEATURE [Part::Cylinder] Cylinder109  label="Cylinder"
  Angle = 360
  AttacherType = Attacher::AttachEngine3D
  Height = 10
  Radius = 1.8
FEATURE [Part::Cone] Cone
  Angle = 360
  AttacherType = Attacher::AttachEngine3D
  Height = 2.5
  Placement = pos=(0,0,7.5) rot=(0,0,1;0rad)
  Radius1 = 1.8
  Radius2 = 3
FEATURE [Part::MultiFuse] Fusion085  label="screw top hole fusion"
  Shapes = -> [Cylinder109,Cone]
FEATURE [App::Part] Part009  label="screw top hole part"
  Group = -> [Cylinder109,Cone,Fusion085]
  Origin = -> Origin081
FEATURE [PartDesign::FeatureBase] Clone052
  BaseFeature = -> Fusion085
FEATURE [PartDesign::Body] Body054  label="screw top hole clone"
  BaseFeature = -> Fusion085
  Group = -> [Clone052]
  Origin = -> Origin082
  Placement = pos=(0,0,0) rot=(0,-1,0;1.5708rad)
  Tip = -> Clone052
FEATURE [Part::FeaturePython] Array001047  label="top screw hole array"  # Draft array (typed FeaturePython)
  Angle = 360
  ArrayType = 0
  Axis = (0,0,1)
  Base = -> Body054
  Center = (0,0,0)
  Fuse = false
  IntervalAxis = (0,0,0)
  IntervalX = (1,0,0)
  IntervalY = (0,25,0)
  IntervalZ = (0,0,20)
  NumberPolar = 1
  NumberX = 1
  NumberY = 2
  NumberZ = 3
  Placement = pos=(0,4,35) rot=(0,0,1;0rad)
  expr: .IntervalY.y = 25
FEATURE [PartDesign::FeatureBase] Clone053
  BaseFeature = -> Array001047
  Placement = pos=(0,4,35) rot=(0,0,1;0rad)
FEATURE [PartDesign::Body] Body055  label="top screw hole array clone"
  BaseFeature = -> Array001047
  Group = -> [Clone053]
  Origin = -> Origin083
  Placement = pos=(17.8,-12,-83) rot=(0,0,1;1.5708rad)
  Tip = -> Clone053
FEATURE [Part::Cut] Cut023020
  Base = -> Box053
  Tool = -> Body055
FEATURE [Part::Chamfer] Chamfer005
  Base = -> Box054
  Edges = 2 edges r=4: [Edge3,Edge7]
FEATURE [Part::MultiFuse] Fusion084
  Shapes = -> [Cut023020,Chamfer005]
FEATURE [Part::Compound] Compound001  label="blocker attached compound"
  Links = -> [Body051,Fusion084]
FEATURE [App::Part] Part008  label="blocker attached part"
  Group = -> [Body051,Fusion084,Box053,Cut023020,Body055,Chamfer005,Box054,Compound001]
  Origin = -> Origin078
